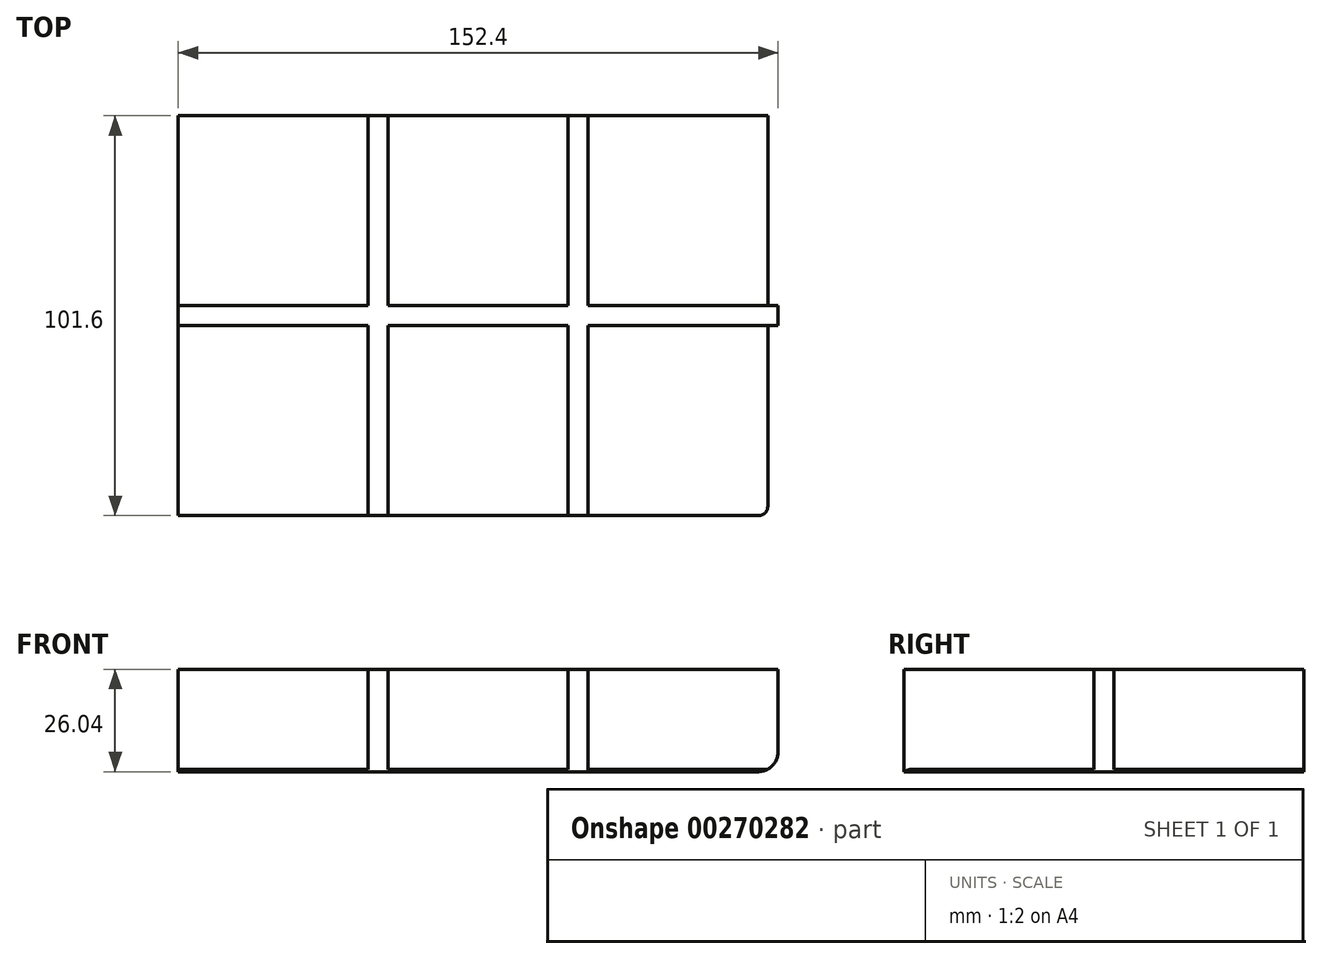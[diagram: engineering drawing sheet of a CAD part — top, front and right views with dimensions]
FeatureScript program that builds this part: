
annotation { "Feature Type Name" : "Feature", "Feature Type Description" : "" }
export const myFeature = defineFeature(function(context is Context, id is Id, definition is map)
    precondition{}
    {
        {
            var Q0;
            Q0=qCreatedBy(makeId("Top.planeOp"),FACE);
            var sketch = newSketch(context, id + "F0", { "sketchPlane" : qUnion([Q0])});
            skLineSegment(sketch, "E0", {"start": v(0, 0) * mm, "end": v(25.4, 0) * mm});
            skLineSegment(sketch, "E1", {"start": v(25.4, 0) * mm, "end": v(25.4, -50.8) * mm});
            skLineSegment(sketch, "E2", {"start": v(25.4, 0) * mm, "end": v(76.2, 0) * mm});
            skLineSegment(sketch, "E3", {"start": v(0, 0) * mm, "end": v(-25.4, 0) * mm});
            skLineSegment(sketch, "E4", {"start": v(-25.4, 0) * mm, "end": v(-76.2, 0) * mm});
            skLineSegment(sketch, "E5", {"start": v(-25.4, 0) * mm, "end": v(-25.4, -50.8) * mm});
            skLineSegment(sketch, "E6", {"start": v(-25.4, 0) * mm, "end": v(-25.4, 50.8) * mm});
            skLineSegment(sketch, "E7", {"start": v(25.4, 0) * mm, "end": v(25.4, 50.8) * mm});
            skLineSegment(sketch, "E8", {"start": v(-25.4, 50.8) * mm, "end": v(25.4, 50.8) * mm});
            skLineSegment(sketch, "E9", {"start": v(76.2, 0) * mm, "end": v(76.2, 50.8) * mm});
            skLineSegment(sketch, "E10", {"start": v(25.4, 50.8) * mm, "end": v(76.2, 50.8) * mm});
            skLineSegment(sketch, "E11", {"start": v(-25.4, 50.8) * mm, "end": v(-76.2, 50.8) * mm});
            skLineSegment(sketch, "E12", {"start": v(-76.2, 0) * mm, "end": v(-76.2, 50.8) * mm});
            skLineSegment(sketch, "E13", {"start": v(-76.2, 0) * mm, "end": v(-76.2, -50.8) * mm});
            skLineSegment(sketch, "E14", {"start": v(-76.2, -50.8) * mm, "end": v(-25.4, -50.8) * mm});
            skLineSegment(sketch, "E15", {"start": v(-25.4, -50.8) * mm, "end": v(25.4, -50.8) * mm});
            skLineSegment(sketch, "E16", {"start": v(25.4, -50.8) * mm, "end": v(76.2, -50.8) * mm});
            skLineSegment(sketch, "E17", {"start": v(76.2, -50.8) * mm, "end": v(76.2, 0) * mm});
            skSolve(sketch);
        }
        {
            var Q0;
            Q0=sQuery(id+"F0.wireOp",EDGE,"E2");
            extrude(context, id + "F1", {"bodyType" : ToolBodyType.SURFACE, "surfaceEntities" : qUnion([Q0]), "depth" : 25.4 * mm});
        }
        {
            var Q0;
            Q0 = qSketchRegion(id + "F0", true);
            var Q1;
            Q1=sQuery(id+"F0.wireOp",EDGE,"E17");
            extrude(context, id + "F2", {"entities" : qUnion([Q0]), "bodyType" : ToolBodyType.SURFACE, "surfaceEntities" : qUnion([Q1]), "depth" : 25.4 * mm});
        }
        {
            var Q0;
            Q0=sQuery(id+"F0.wireOp",EDGE,"E1");
            extrude(context, id + "F3", {"bodyType" : ToolBodyType.SURFACE, "surfaceEntities" : qUnion([Q0]), "depth" : 25.4 * mm});
        }
        {
            var Q0;
            Q0 = qSketchRegion(id + "F0", true);
            var Q1;
            Q1=sQuery(id+"F0.wireOp",EDGE,"E16");
            extrude(context, id + "F4", {"entities" : qUnion([Q0]), "bodyType" : ToolBodyType.SURFACE, "surfaceEntities" : qUnion([Q1]), "depth" : 25.4 * mm});
        }
        {
            var Q0;
            Q0=sQuery(id+"F0.wireOp",EDGE,"E9");
            extrude(context, id + "F5", {"bodyType" : ToolBodyType.SURFACE, "surfaceEntities" : qUnion([Q0]), "depth" : 25.4 * mm});
        }
        {
            var Q0;
            Q0 = qSketchRegion(id + "F0", true);
            var Q1;
            Q1=sQuery(id+"F0.wireOp",EDGE,"E10");
            extrude(context, id + "F6", {"entities" : qUnion([Q0]), "bodyType" : ToolBodyType.SURFACE, "surfaceEntities" : qUnion([Q1]), "depth" : 25.4 * mm});
        }
        {
            var Q0;
            Q0 = qSketchRegion(id + "F0", true);
            var Q1;
            Q1=sQuery(id+"F0.wireOp",EDGE,"E7");
            extrude(context, id + "F7", {"entities" : qUnion([Q0]), "bodyType" : ToolBodyType.SURFACE, "surfaceEntities" : qUnion([Q1]), "depth" : 25.4 * mm});
        }
        {
            var Q0;
            Q0=sQuery(id+"F0.wireOp",EDGE,"E8");
            extrude(context, id + "F8", {"bodyType" : ToolBodyType.SURFACE, "surfaceEntities" : qUnion([Q0]), "depth" : 25.4 * mm});
        }
        {
            var Q0;
            Q0=sQuery(id+"F0.wireOp",EDGE,"E0");
            var Q1;
            Q1=sQuery(id+"F0.wireOp",EDGE,"E3");
            extrude(context, id + "F9", {"bodyType" : ToolBodyType.SURFACE, "surfaceEntities" : qUnion([Q0, Q1]), "depth" : 25.4 * mm});
        }
        {
            var Q0;
            Q0=sQuery(id+"F0.wireOp",EDGE,"E15");
            extrude(context, id + "F10", {"bodyType" : ToolBodyType.SURFACE, "surfaceEntities" : qUnion([Q0]), "depth" : 25.4 * mm});
        }
        {
            var Q0;
            Q0=sQuery(id+"F0.wireOp",EDGE,"E6");
            var Q1;
            Q1=sQuery(id+"F0.wireOp",EDGE,"E5");
            extrude(context, id + "F11", {"bodyType" : ToolBodyType.SURFACE, "surfaceEntities" : qUnion([Q0, Q1]), "depth" : 25.4 * mm});
        }
        {
            var Q0;
            Q0=sQuery(id+"F0.wireOp",EDGE,"E11");
            extrude(context, id + "F12", {"bodyType" : ToolBodyType.SURFACE, "surfaceEntities" : qUnion([Q0]), "depth" : 25.4 * mm});
        }
        {
            var Q0;
            Q0=sQuery(id+"F0.wireOp",EDGE,"E4");
            extrude(context, id + "F13", {"bodyType" : ToolBodyType.SURFACE, "surfaceEntities" : qUnion([Q0]), "depth" : 25.4 * mm});
        }
        {
            var Q0;
            Q0 = qSketchRegion(id + "F0", true);
            var Q1;
            Q1=sQuery(id+"F0.wireOp",EDGE,"E12");
            var Q2;
            Q2=sQuery(id+"F0.wireOp",EDGE,"E13");
            extrude(context, id + "F14", {"entities" : qUnion([Q0]), "bodyType" : ToolBodyType.SURFACE, "operationType" : NewBodyOperationType.INTERSECT, "surfaceEntities" : qUnion([Q1, Q2]), "depth" : 25.4 * mm});
        }
        {
            var Q0;
            Q0 = qSketchRegion(id + "F0", true);
            var Q1;
            Q1=sQuery(id+"F0.wireOp",EDGE,"E14");
            extrude(context, id + "F15", {"entities" : qUnion([Q0]), "bodyType" : ToolBodyType.SURFACE, "surfaceEntities" : qUnion([Q1]), "depth" : 25.4 * mm});
        }
        {
            var Q0;
            Q0 = qSketchRegion(id + "F0", true);
            extrude(context, id + "F16", {"entities" : qUnion([Q0]), "oppositeDirection" : true, "depth" : 0.64 * mm});
        }
        {
            var Q0;
            Q0=makeQuery(id+"F13.opExtrude","SWEPT_FACE",FACE,{"disambiguationData":[OSD([sQuery(id+"F0.wireOp",EDGE,"E4")])]});
            extrude(context, id + "F17", {"entities" : qUnion([Q0]), "operationType" : NewBodyOperationType.ADD, "endBound" : BoundingType.SYMMETRIC, "depth" : 5.08 * mm});
        }
        {
            var Q0;
            Q0=makeQuery(id+"F11.opExtrude","SWEPT_FACE",FACE,{"disambiguationData":[OSD([sQuery(id+"F0.wireOp",EDGE,"E5"),sQuery(id+"F0.wireOp",EDGE,"E6")])]});
            extrude(context, id + "F18", {"entities" : qUnion([Q0]), "operationType" : NewBodyOperationType.ADD, "endBound" : BoundingType.SYMMETRIC, "depth" : 5.08 * mm});
        }
        {
            var Q0;
            Q0=makeQuery(id+"F9.opExtrude","SWEPT_FACE",FACE,{"disambiguationData":[OSD([sQuery(id+"F0.wireOp",EDGE,"E0"),sQuery(id+"F0.wireOp",EDGE,"E3")])]});
            extrude(context, id + "F19", {"entities" : qUnion([Q0]), "operationType" : NewBodyOperationType.ADD, "endBound" : BoundingType.SYMMETRIC, "depth" : 5.08 * mm});
        }
        {
            var Q0;
            Q0=makeQuery(id+"F7.opExtrude","SWEPT_FACE",FACE,{"disambiguationData":[OSD([sQuery(id+"F0.wireOp",EDGE,"E7")])]});
            extrude(context, id + "F20", {"entities" : qUnion([Q0]), "operationType" : NewBodyOperationType.ADD, "endBound" : BoundingType.SYMMETRIC, "depth" : 5.08 * mm});
        }
        {
            var Q0;
            Q0=makeQuery(id+"F3.opExtrude","SWEPT_FACE",FACE,{"disambiguationData":[OSD([sQuery(id+"F0.wireOp",EDGE,"E1")])]});
            extrude(context, id + "F21", {"entities" : qUnion([Q0]), "operationType" : NewBodyOperationType.ADD, "endBound" : BoundingType.SYMMETRIC, "depth" : 5.08 * mm});
        }
        {
            var Q0;
            Q0=makeQuery(id+"F1.opExtrude","SWEPT_FACE",FACE,{"disambiguationData":[OSD([sQuery(id+"F0.wireOp",EDGE,"E2")])]});
            extrude(context, id + "F22", {"entities" : qUnion([Q0]), "operationType" : NewBodyOperationType.ADD, "endBound" : BoundingType.SYMMETRIC, "depth" : 5.08 * mm});
        }
        {
            var Q0;
            Q0=makeQuery(id+"F16.opExtrude","CAP_EDGE",EDGE,{"disambiguationData":[OSD([sQuery(id+"F0.wireOp",EDGE,"E9"),sQuery(id+"F0.wireOp",EDGE,"E17")])],"isStart":false});
            fillet(context, id + "F23", {"entities" : qUnion([Q0]), "radius" : 5.08 * mm, "tangentPropagation" : true, "allowEdgeOverflow" : false});
        }
        {
            var Q0;
            {var subQ1=sQuery(id+"F0.wireOp",EDGE,"E17");var subQ2=sQuery(id+"F0.wireOp",EDGE,"E9");var subQ3=makeQuery(id+"F16.opExtrude","SWEPT_FACE",FACE,{"disambiguationData":[OSD([subQ2,subQ1])]});var subQ4=sQuery(id+"F0.wireOp",EDGE,"E16");var subQ5=sQuery(id+"F0.wireOp",EDGE,"E15");var subQ6=sQuery(id+"F0.wireOp",EDGE,"E14");Q0=makeQuery(id+"F21.boolean.opBoolean","SPLIT",EDGE,{"disambiguationData":[TD([makeQuery(id+"F20.opExtrude","CAP_FACE",FACE,{"disambiguationData":[OSD([sQuery(id+"F0.wireOp",EDGE,"E7")])],"isStart":false})])],"derivedFrom":makeQuery(id+"F18.boolean.opBoolean","SPLIT",EDGE,{"disambiguationData":[TD([subQ3])],"derivedFrom":makeQuery(id+"F16.opExtrude","CAP_EDGE",EDGE,{"disambiguationData":[OSD([subQ6,subQ5,subQ4])],"isStart":true})})});}
            fillet(context, id + "F24", {"entities" : qUnion([Q0]), "radius" : 5.08 * mm, "tangentPropagation" : true, "allowEdgeOverflow" : false});
        }
    });
